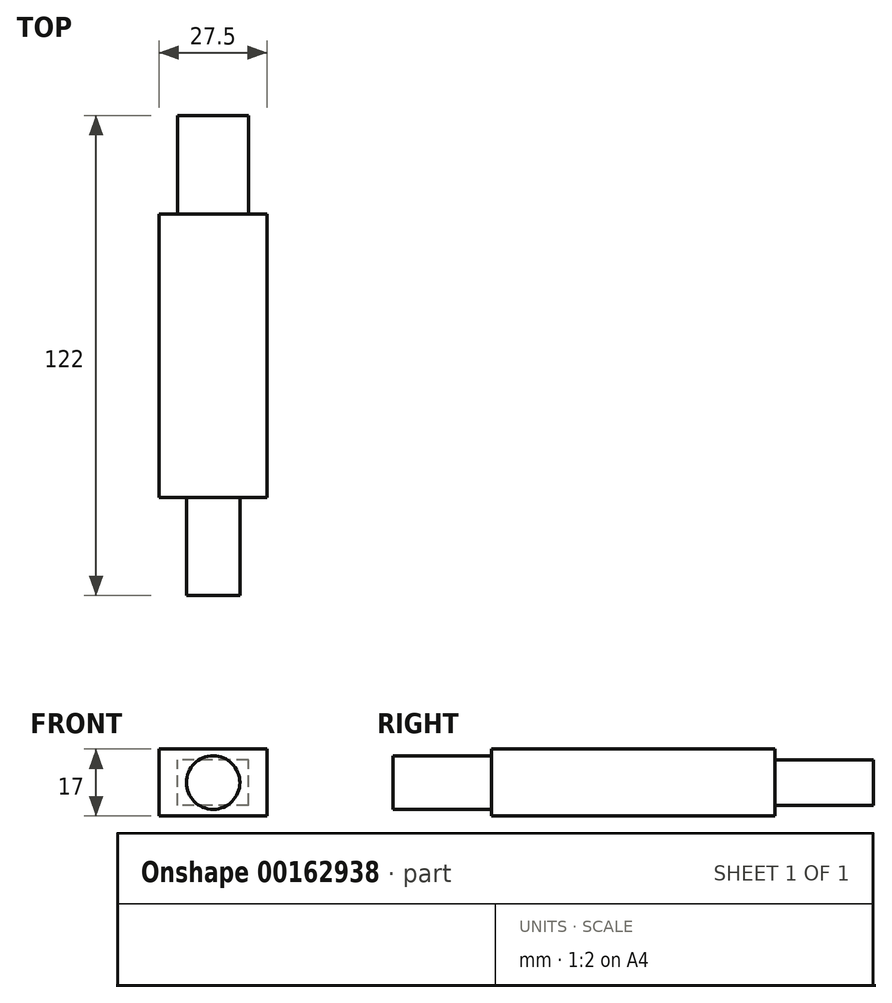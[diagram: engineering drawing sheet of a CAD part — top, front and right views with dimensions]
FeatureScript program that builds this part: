
annotation { "Feature Type Name" : "Feature", "Feature Type Description" : "" }
export const myFeature = defineFeature(function(context is Context, id is Id, definition is map)
    precondition{}
    {
        {
            var Q0;
            Q0=qCreatedBy(makeId("Top.planeOp"),FACE);
            var sketch = newSketch(context, id + "F0", { "sketchPlane" : qUnion([Q0])});
            skLineSegment(sketch, "E0.bottom", {"start": v(13.75, 36) * mm, "end": v(-13.75, 36) * mm});
            skLineSegment(sketch, "E0.top", {"start": v(13.75, -36) * mm, "end": v(-13.75, -36) * mm});
            skLineSegment(sketch, "E0.left", {"start": v(13.75, 36) * mm, "end": v(13.75, -36) * mm});
            skLineSegment(sketch, "E0.right", {"start": v(-13.75, 36) * mm, "end": v(-13.75, -36) * mm});
            skPoint(sketch, "E0.middle", {"position": v(0, 0) * mm});
            skSolve(sketch);
        }
        {
            var Q0;
            Q0=makeQuery(id+"F0.imprint","IMPRINT",FACE,{"disambiguationData":[TD([[makeQuery(id+"F0.imprint","IMPRINT",EDGE,{"derivedFrom":sQuery(id+"F0.wireOp",EDGE,"E0.bottom")}),1.0]])]});
            extrude(context, id + "F1", {"entities" : qUnion([Q0]), "depth" : 17 * mm});
        }
        {
            var Q0;
            Q0=makeQuery(id+"F1.opExtrude","SWEPT_FACE",FACE,{"disambiguationData":[OSD([sQuery(id+"F0.wireOp",EDGE,"E0.bottom")])]});
            var sketch = newSketch(context, id + "F2", { "sketchPlane" : qUnion([Q0])});
            skLineSegment(sketch, "E1.bottom", {"start": v(-9, 2.75) * mm, "end": v(9, 2.75) * mm});
            skLineSegment(sketch, "E1.top", {"start": v(-9, 14.25) * mm, "end": v(9, 14.25) * mm});
            skLineSegment(sketch, "E1.left", {"start": v(-9, 2.75) * mm, "end": v(-9, 14.25) * mm});
            skLineSegment(sketch, "E1.right", {"start": v(9, 2.75) * mm, "end": v(9, 14.25) * mm});
            skPoint(sketch, "E1.middle", {"position": v(0, 8.5) * mm});
            skPoint(sketch, "E1.middle.positionSnap0", {"position": v(13.75, 8.5) * mm});
            skPoint(sketch, "E1.centerSnap0", {"position": v(13.75, 8.5) * mm});
            skSolve(sketch);
        }
        {
            var Q0;
            Q0=makeQuery(id+"F2.imprint","IMPRINT",FACE,{"disambiguationData":[TD([[makeQuery(id+"F2.imprint","IMPRINT",EDGE,{"derivedFrom":sQuery(id+"F2.wireOp",EDGE,"E1.bottom")}),1.0]])]});
            extrude(context, id + "F3", {"entities" : qUnion([Q0]), "operationType" : NewBodyOperationType.ADD, "depth" : 25 * mm});
        }
        {
            var Q0;
            Q0=makeQuery(id+"F1.opExtrude","SWEPT_FACE",FACE,{"disambiguationData":[OSD([sQuery(id+"F0.wireOp",EDGE,"E0.top")])]});
            var sketch = newSketch(context, id + "F4", { "sketchPlane" : qUnion([Q0])});
            skCircle(sketch, "E2", {"center": v(0, 8.5) * mm, "radius": 6.8 * mm});
            skPoint(sketch, "E2.centerSnap0", {"position": v(13.75, 8.5) * mm});
            skPoint(sketch, "E2.centerSnap1", {"position": v(0, 17) * mm});
            skSolve(sketch);
        }
        {
            var Q0;
            Q0=makeQuery(id+"F4.imprint","IMPRINT",FACE,{"disambiguationData":[TD([[makeQuery(id+"F4.imprint","IMPRINT",EDGE,{"derivedFrom":sQuery(id+"F4.wireOp",EDGE,"E2")}),1.0]])]});
            extrude(context, id + "F5", {"entities" : qUnion([Q0]), "operationType" : NewBodyOperationType.ADD, "depth" : 25 * mm});
        }
    });
